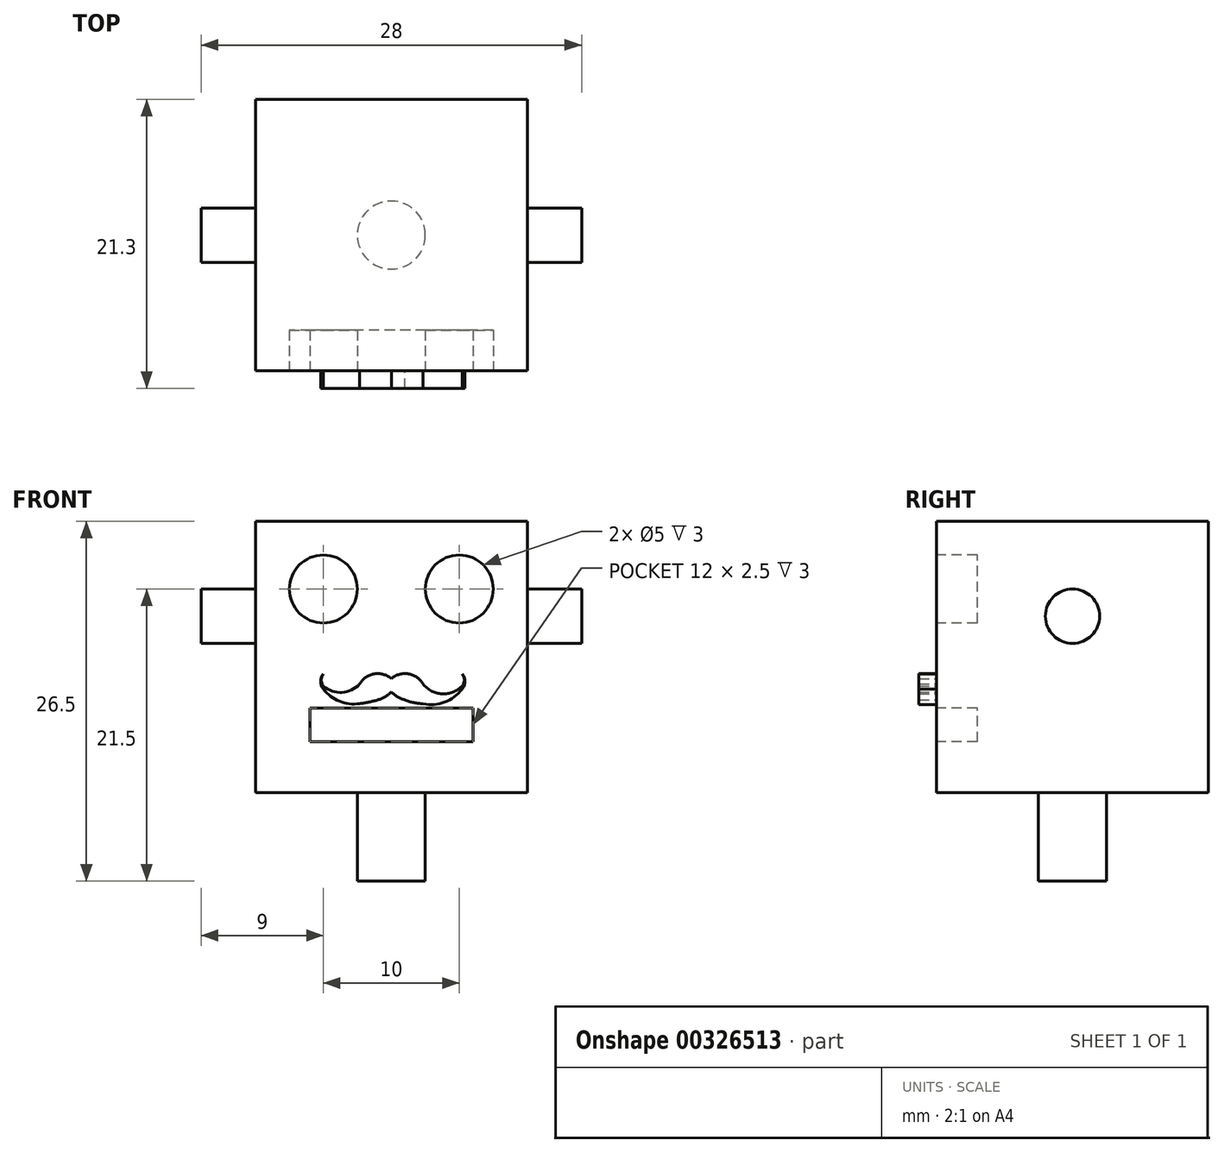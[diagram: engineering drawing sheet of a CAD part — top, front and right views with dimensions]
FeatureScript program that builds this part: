
annotation { "Feature Type Name" : "Feature", "Feature Type Description" : "" }
export const myFeature = defineFeature(function(context is Context, id is Id, definition is map)
    precondition{}
    {
        {
            var Q0;
            Q0=qCreatedBy(makeId("Front.planeOp"),FACE);
            var sketch = newSketch(context, id + "F0", { "sketchPlane" : qUnion([Q0])});
            skLineSegment(sketch, "E0.bottom", {"start": v(10, -10) * mm, "end": v(-10, -10) * mm});
            skLineSegment(sketch, "E0.top", {"start": v(10, 10) * mm, "end": v(-10, 10) * mm});
            skLineSegment(sketch, "E0.left", {"start": v(10, -10) * mm, "end": v(10, 10) * mm});
            skLineSegment(sketch, "E0.right", {"start": v(-10, -10) * mm, "end": v(-10, 10) * mm});
            skPoint(sketch, "E0.middle", {"position": v(0, 0) * mm});
            skSolve(sketch);
        }
        {
            var Q0;
            Q0 = qSketchRegion(id + "F0", true);
            extrude(context, id + "F1", {"entities" : qUnion([Q0]), "depth" : 20 * mm});
        }
        {
            var Q0;
            Q0=makeQuery(id+"F1.opExtrude","CAP_FACE",FACE,{"disambiguationData":[OSD([sQuery(id+"F0.wireOp",EDGE,"E0.bottom"),sQuery(id+"F0.wireOp",EDGE,"E0.top"),sQuery(id+"F0.wireOp",EDGE,"E0.left"),sQuery(id+"F0.wireOp",EDGE,"E0.right")])],"isStart":false});
            var sketch = newSketch(context, id + "F2", { "sketchPlane" : qUnion([Q0])});
            skLineSegment(sketch, "E1", {"start": v(-10, 0) * mm, "end": v(0, 10) * mm, "construction": true});
            skLineSegment(sketch, "E2", {"start": v(0, 0) * mm, "end": v(10, 10) * mm, "construction": true});
            skCircle(sketch, "E3", {"center": v(-5, 5) * mm, "radius": 2.5 * mm});
            skCircle(sketch, "E4", {"center": v(5, 5) * mm, "radius": 2.5 * mm});
            skLineSegment(sketch, "E5", {"start": v(0, 0) * mm, "end": v(0, -10) * mm, "construction": true});
            skLineSegment(sketch, "E6.bottom", {"start": v(6, -6.25) * mm, "end": v(-6, -6.25) * mm});
            skLineSegment(sketch, "E6.top", {"start": v(6, -3.75) * mm, "end": v(-6, -3.75) * mm});
            skLineSegment(sketch, "E6.left", {"start": v(6, -6.25) * mm, "end": v(6, -3.75) * mm});
            skLineSegment(sketch, "E6.right", {"start": v(-6, -6.25) * mm, "end": v(-6, -3.75) * mm});
            skPoint(sketch, "E6.middle", {"position": v(0, -5) * mm});
            skSolve(sketch);
        }
        {
            var Q0;
            Q0 = qSketchRegion(id + "F2", true);
            extrude(context, id + "F3", {"entities" : qUnion([Q0]), "operationType" : NewBodyOperationType.REMOVE, "oppositeDirection" : true, "depth" : 3 * mm});
        }
        {
            var Q0;
            Q0=makeQuery(id+"F1.opExtrude","SWEPT_FACE",FACE,{"disambiguationData":[OSD([sQuery(id+"F0.wireOp",EDGE,"E0.left")])]});
            var sketch = newSketch(context, id + "F4", { "sketchPlane" : qUnion([Q0])});
            skCircle(sketch, "E7", {"center": v(-10, 3) * mm, "radius": 2 * mm});
            skSolve(sketch);
        }
        {
            var Q0;
            Q0 = qSketchRegion(id + "F4", true);
            extrude(context, id + "F5", {"entities" : qUnion([Q0]), "operationType" : NewBodyOperationType.ADD, "depth" : 4 * mm});
        }
        {
            var Q0;
            Q0=makeQuery(id+"F1.opExtrude","SWEPT_FACE",FACE,{"disambiguationData":[OSD([sQuery(id+"F0.wireOp",EDGE,"E0.right")])]});
            var sketch = newSketch(context, id + "F6", { "sketchPlane" : qUnion([Q0])});
            skCircle(sketch, "E8", {"center": v(10, 3) * mm, "radius": 2 * mm});
            skSolve(sketch);
        }
        {
            var Q0;
            Q0 = qSketchRegion(id + "F6", true);
            extrude(context, id + "F7", {"entities" : qUnion([Q0]), "operationType" : NewBodyOperationType.ADD, "depth" : 4 * mm});
        }
        {
            var Q0;
            Q0=makeQuery(id+"F1.opExtrude","SWEPT_FACE",FACE,{"disambiguationData":[OSD([sQuery(id+"F0.wireOp",EDGE,"E0.bottom")])]});
            var sketch = newSketch(context, id + "F8", { "sketchPlane" : qUnion([Q0])});
            skCircle(sketch, "E9", {"center": v(0, 10) * mm, "radius": 2.5 * mm});
            skSolve(sketch);
        }
        {
            var Q0;
            Q0=makeQuery(id+"F8.imprint","IMPRINT",FACE,{"disambiguationData":[TD([[makeQuery(id+"F8.imprint","IMPRINT",EDGE,{"derivedFrom":sQuery(id+"F8.wireOp",EDGE,"E9")}),1.0]])]});
            extrude(context, id + "F9", {"entities" : qUnion([Q0]), "operationType" : NewBodyOperationType.ADD, "depth" : 6.5 * mm});
        }
        {
            var Q0;
            Q0=makeQuery(id+"F1.opExtrude","CAP_FACE",FACE,{"disambiguationData":[OSD([sQuery(id+"F0.wireOp",EDGE,"E0.bottom"),sQuery(id+"F0.wireOp",EDGE,"E0.top"),sQuery(id+"F0.wireOp",EDGE,"E0.left"),sQuery(id+"F0.wireOp",EDGE,"E0.right")])],"isStart":false});
            var sketch = newSketch(context, id + "F10", { "sketchPlane" : qUnion([Q0])});
            skArc(sketch, "E10", {"start": v(0, -1.59) * mm, "mid": v(-1.26, -1.25) * mm, "end": v(-2.33, -2) * mm});
            skArc(sketch, "E11", {"start": v(2.33, -2) * mm, "mid": v(1.26, -1.25) * mm, "end": v(0, -1.59) * mm});
            skArc(sketch, "E12", {"start": v(-4.99, -2.14) * mm, "mid": v(-3.63, -2.6) * mm, "end": v(-2.33, -2) * mm});
            skArc(sketch, "E13", {"start": v(2.33, -2) * mm, "mid": v(3.74, -2.72) * mm, "end": v(5.2, -2.14) * mm});
            skArc(sketch, "E14", {"start": v(-4.99, -1.25) * mm, "mid": v(-5.15, -1.7) * mm, "end": v(-4.99, -2.14) * mm});
            skPoint(sketch, "E14.startSnap0", {"position": v(-1.26, -1.25) * mm});
            skArc(sketch, "E15", {"start": v(-4.99, -1.25) * mm, "mid": v(-5.2, -1.8) * mm, "end": v(-4.99, -2.36) * mm});
            skArc(sketch, "E16", {"start": v(-4.99, -2.36) * mm, "mid": v(-3.8, -3.27) * mm, "end": v(-2.33, -3.44) * mm});
            skPoint(sketch, "E17", {"position": v(1.26, -1.25) * mm});
            skArc(sketch, "E18", {"start": v(5.2, -2.14) * mm, "mid": v(5.36, -1.7) * mm, "end": v(5.2, -1.25) * mm});
            skArc(sketch, "E19", {"start": v(5.2, -2.36) * mm, "mid": v(5.42, -1.8) * mm, "end": v(5.2, -1.25) * mm});
            skArc(sketch, "E20", {"start": v(2.33, -3.44) * mm, "mid": v(3.93, -3.33) * mm, "end": v(5.2, -2.36) * mm});
            skArc(sketch, "E21", {"start": v(-2.33, -3.44) * mm, "mid": v(-1.66, -3.33) * mm, "end": v(-1, -3.16) * mm});
            skArc(sketch, "E22", {"start": v(-1, -3.16) * mm, "mid": v(-0.46, -2.93) * mm, "end": v(0, -2.58) * mm});
            skArc(sketch, "E23", {"start": v(1, -3.16) * mm, "mid": v(1.65, -3.36) * mm, "end": v(2.33, -3.44) * mm});
            skArc(sketch, "E24", {"start": v(0, -2.58) * mm, "mid": v(0.46, -2.93) * mm, "end": v(1, -3.16) * mm});
            skSolve(sketch);
        }
        {
            var Q0;
            Q0=makeQuery(id+"F10.imprint","IMPRINT",FACE,{"disambiguationData":[TD([[makeQuery(id+"F10.imprint","IMPRINT",EDGE,{"derivedFrom":sQuery(id+"F10.wireOp",EDGE,"E10")}),1.0]])]});
            extrude(context, id + "F11", {"entities" : qUnion([Q0]), "operationType" : NewBodyOperationType.ADD, "depth" : 1.3 * mm});
        }
    });
